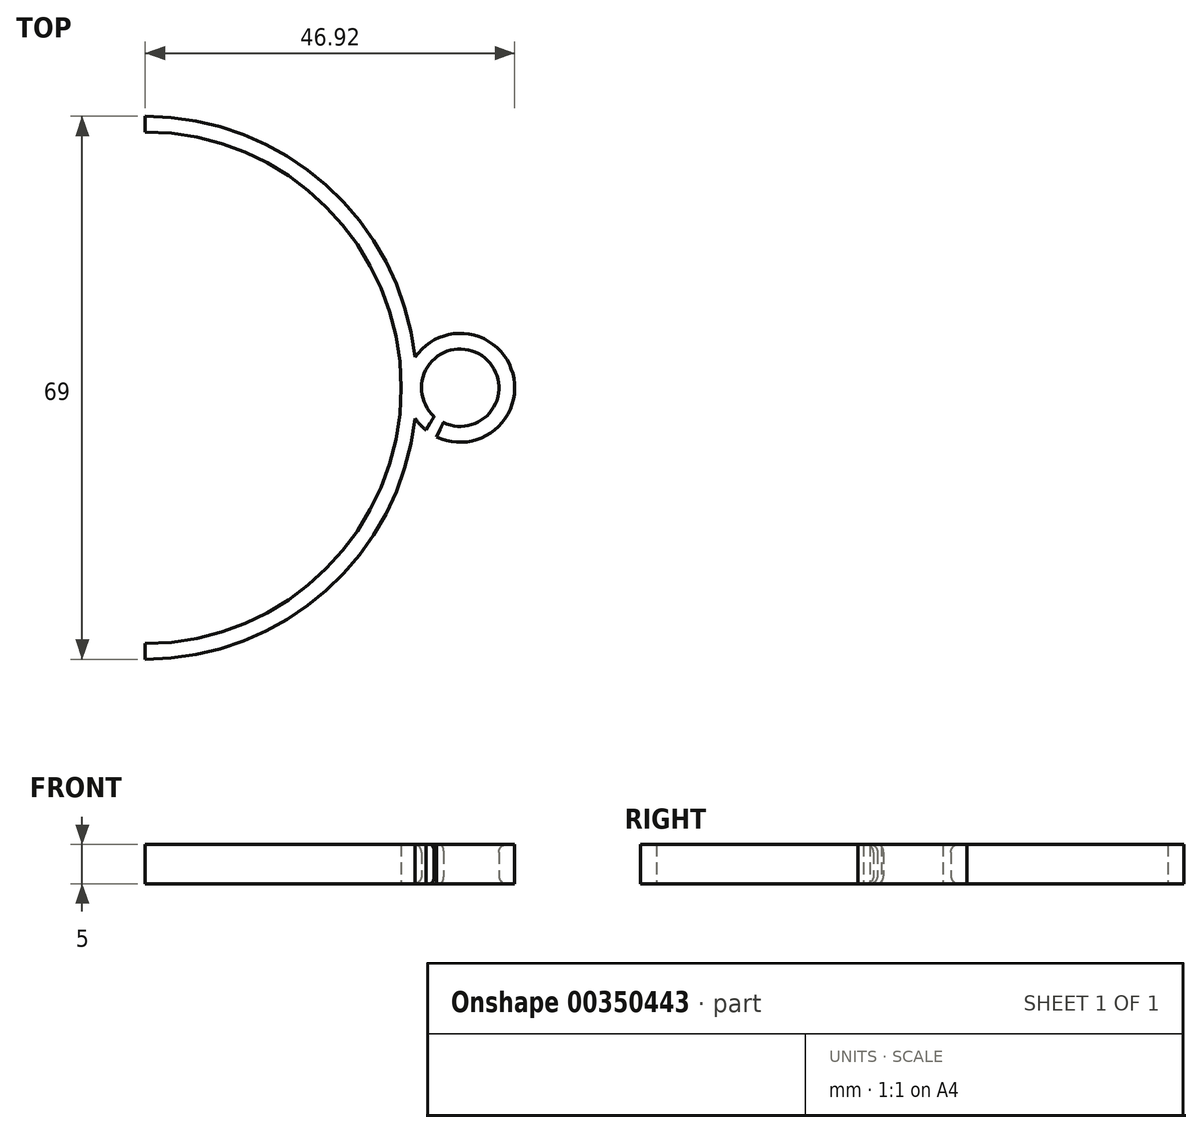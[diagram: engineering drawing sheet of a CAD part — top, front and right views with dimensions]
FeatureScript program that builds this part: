
annotation { "Feature Type Name" : "Feature", "Feature Type Description" : "" }
export const myFeature = defineFeature(function(context is Context, id is Id, definition is map)
    precondition{}
    {
        {
            var Q0;
            Q0=qCreatedBy(makeId("Top.planeOp"),FACE);
            var sketch = newSketch(context, id + "F0", { "sketchPlane" : qUnion([Q0])});
            skArc(sketch, "E0", {"start": v(0, 32.5) * mm, "mid": v(32.5, 0) * mm, "end": v(0, -32.5) * mm});
            skArc(sketch, "E1.0", {"start": v(0, 34.5) * mm, "mid": v(34.5, 0) * mm, "end": v(0, -34.5) * mm});
            skLineSegment(sketch, "E2", {"start": v(0, 34.5) * mm, "end": v(0, 32.5) * mm});
            skLineSegment(sketch, "E3", {"start": v(0, -34.5) * mm, "end": v(0, -32.5) * mm});
            skSolve(sketch);
        }
        {
            var Q0;
            Q0 = qSketchRegion(id + "F0", true);
            extrude(context, id + "F1", {"entities" : qUnion([Q0]), "depth" : 5 * mm});
        }
        {
            var Q0;
            Q0=qCreatedBy(makeId("Top.planeOp"),FACE);
            var sketch = newSketch(context, id + "F2", { "sketchPlane" : qUnion([Q0])});
            skArc(sketch, "E4", {"start": v(36.99, -6.23) * mm, "mid": v(43.72, 5.83) * mm, "end": v(35.63, -5.36) * mm});
            skArc(sketch, "E5.0", {"start": v(37.86, -4.43) * mm, "mid": v(42.75, 4.08) * mm, "end": v(36.7, -3.65) * mm});
            skLineSegment(sketch, "E6", {"start": v(37.86, -4.43) * mm, "end": v(36.99, -6.23) * mm});
            skLineSegment(sketch, "E7", {"start": v(36.7, -3.65) * mm, "end": v(35.63, -5.36) * mm});
            skSolve(sketch);
        }
        {
            var Q0;
            Q0=makeQuery(id+"F2.imprint","IMPRINT",FACE,{"disambiguationData":[TD([[makeQuery(id+"F2.imprint","IMPRINT",EDGE,{"derivedFrom":sQuery(id+"F2.wireOp",EDGE,"E4")}),1.0]])]});
            extrude(context, id + "F3", {"entities" : qUnion([Q0]), "operationType" : NewBodyOperationType.ADD, "depth" : 5 * mm});
        }
        {
            var Q0;
            Q0=makeQuery(id+"F3.opExtrude","CAP_EDGE",EDGE,{"disambiguationData":[OSD([sQuery(id+"F2.wireOp",EDGE,"E5.0")])],"isStart":true});
            var Q1;
            Q1=makeQuery(id+"F3.opExtrude","CAP_EDGE",EDGE,{"disambiguationData":[OSD([sQuery(id+"F2.wireOp",EDGE,"E5.0")])],"isStart":false});
            fillet(context, id + "F4", {"entities" : qUnion([Q0, Q1]), "radius" : 1 * mm, "tangentPropagation" : true, "allowEdgeOverflow" : false});
        }
    });
